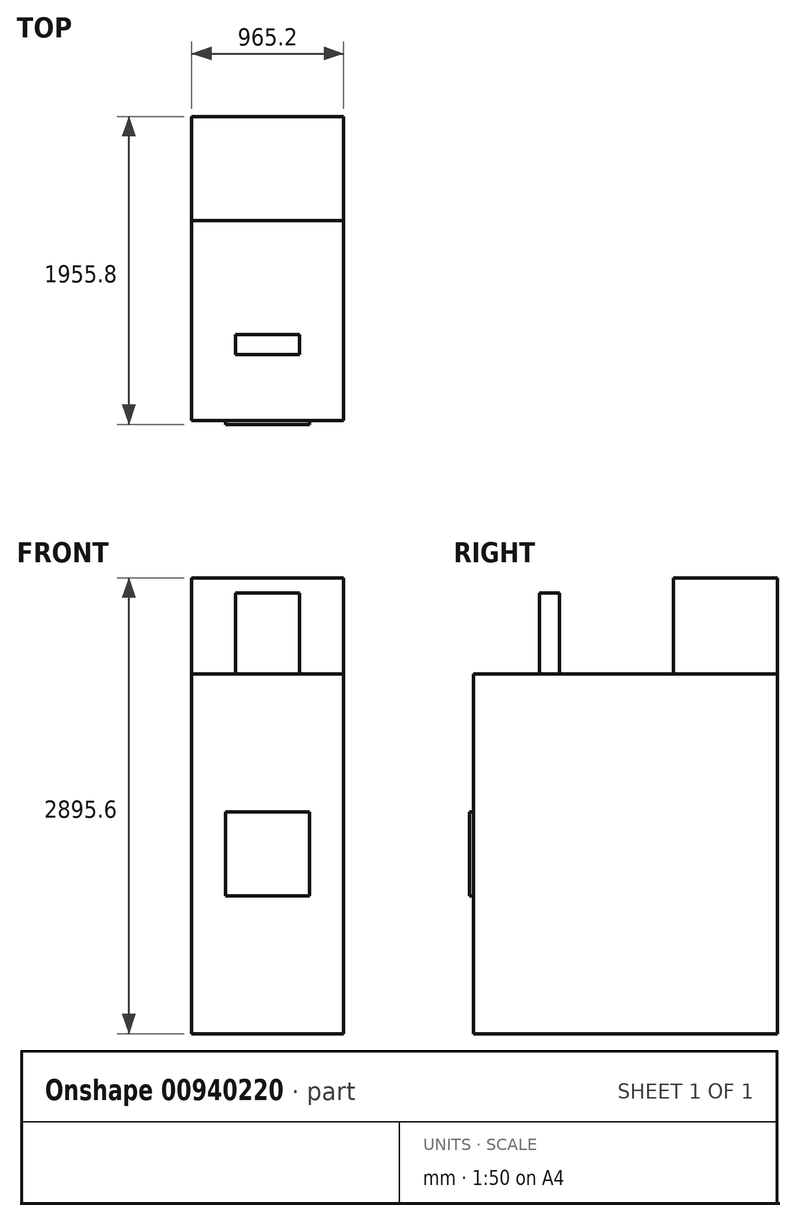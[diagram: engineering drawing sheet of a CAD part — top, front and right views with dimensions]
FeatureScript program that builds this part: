
annotation { "Feature Type Name" : "Feature", "Feature Type Description" : "" }
export const myFeature = defineFeature(function(context is Context, id is Id, definition is map)
    precondition{}
    {
        {
            var Q0;
            Q0=qCreatedBy(makeId("Front.planeOp"),FACE);
            var sketch = newSketch(context, id + "F0", { "sketchPlane" : qUnion([Q0])});
            skLineSegment(sketch, "E0.bottom", {"start": v(0, 0) * mm, "end": v(965.2, 0) * mm});
            skLineSegment(sketch, "E0.top", {"start": v(0, 2286) * mm, "end": v(965.2, 2286) * mm});
            skLineSegment(sketch, "E0.left", {"start": v(0, 0) * mm, "end": v(0, 2286) * mm});
            skLineSegment(sketch, "E0.right", {"start": v(965.2, 0) * mm, "end": v(965.2, 2286) * mm});
            skSolve(sketch);
        }
        {
            var Q0;
            Q0=makeQuery(id+"F0.imprint","IMPRINT",FACE,{"disambiguationData":[TD([[makeQuery(id+"F0.imprint","IMPRINT",EDGE,{"derivedFrom":sQuery(id+"F0.wireOp",EDGE,"E0.bottom")}),1.0]])]});
            extrude(context, id + "F1", {"entities" : qUnion([Q0]), "oppositeDirection" : true, "depth" : 965.2 * mm, "offsetDistance" : 25.4 * mm});
        }
        {
            var Q0;
            Q0=makeQuery(id+"F1.opExtrude","CAP_FACE",FACE,{"disambiguationData":[OSD([sQuery(id+"F0.wireOp",EDGE,"E0.bottom"),sQuery(id+"F0.wireOp",EDGE,"E0.top"),sQuery(id+"F0.wireOp",EDGE,"E0.left"),sQuery(id+"F0.wireOp",EDGE,"E0.right")])],"isStart":false});
            extrude(context, id + "F2", {"entities" : qUnion([Q0]), "depth" : 965.2 * mm, "offsetDistance" : 25.4 * mm});
        }
        {
            var Q0;
            Q0=makeQuery(id+"F1.opExtrude","SWEPT_FACE",FACE,{"disambiguationData":[OSD([sQuery(id+"F0.wireOp",EDGE,"E0.top")])]});
            var sketch = newSketch(context, id + "F3", { "sketchPlane" : qUnion([Q0])});
            skLineSegment(sketch, "E1.bottom", {"start": v(685.8, 419.1) * mm, "end": v(279.4, 419.1) * mm});
            skLineSegment(sketch, "E1.top", {"start": v(685.8, 546.1) * mm, "end": v(279.4, 546.1) * mm});
            skLineSegment(sketch, "E1.left", {"start": v(685.8, 419.1) * mm, "end": v(685.8, 546.1) * mm});
            skLineSegment(sketch, "E1.right", {"start": v(279.4, 419.1) * mm, "end": v(279.4, 546.1) * mm});
            skPoint(sketch, "E1.middle", {"position": v(482.6, 482.6) * mm});
            skPoint(sketch, "E1.middle.positionSnap0", {"position": v(965.2, 482.6) * mm});
            skPoint(sketch, "E1.middle.positionSnap1", {"position": v(482.6, 0) * mm});
            skPoint(sketch, "E1.centerSnap0", {"position": v(965.2, 482.6) * mm});
            skPoint(sketch, "E1.centerSnap1", {"position": v(482.6, 0) * mm});
            skSolve(sketch);
        }
        {
            var Q0;
            Q0=makeQuery(id+"F3.imprint","IMPRINT",FACE,{"disambiguationData":[TD([[makeQuery(id+"F3.imprint","IMPRINT",EDGE,{"derivedFrom":sQuery(id+"F3.wireOp",EDGE,"E1.bottom")}),-1.0]])]});
            extrude(context, id + "F4", {"entities" : qUnion([Q0]), "depth" : 513.08 * mm, "offsetDistance" : 25.4 * mm});
        }
        {
            var Q0;
            Q0=qCreatedBy(makeId("Front.planeOp"),FACE);
            var sketch = newSketch(context, id + "F5", { "sketchPlane" : qUnion([Q0])});
            skLineSegment(sketch, "E2", {"start": v(0, 0) * mm, "end": v(0, 1143) * mm, "construction": true});
            skLineSegment(sketch, "E3", {"start": v(0, 1143) * mm, "end": v(482.6, 1143) * mm, "construction": true});
            skLineSegment(sketch, "E4.bottom", {"start": v(749.3, 876.3) * mm, "end": v(215.9, 876.3) * mm});
            skLineSegment(sketch, "E4.top", {"start": v(749.3, 1409.7) * mm, "end": v(215.9, 1409.7) * mm});
            skLineSegment(sketch, "E4.left", {"start": v(749.3, 876.3) * mm, "end": v(749.3, 1409.7) * mm});
            skLineSegment(sketch, "E4.right", {"start": v(215.9, 876.3) * mm, "end": v(215.9, 1409.7) * mm});
            skPoint(sketch, "E4.middle", {"position": v(482.6, 1143) * mm});
            skSolve(sketch);
        }
        {
            var Q0;
            Q0=makeQuery(id+"F5.imprint","IMPRINT",FACE,{"disambiguationData":[TD([[makeQuery(id+"F5.imprint","IMPRINT",EDGE,{"derivedFrom":sQuery(id+"F5.wireOp",EDGE,"E4.bottom")}),-1.0]])]});
            extrude(context, id + "F6", {"entities" : qUnion([Q0]), "oppositeDirection" : true, "depth" : 482.6 * mm, "offsetDistance" : 25.4 * mm});
        }
        {
            var Q0;
            Q0=makeQuery(id+"F5.imprint","IMPRINT",FACE,{"disambiguationData":[TD([[makeQuery(id+"F5.imprint","IMPRINT",EDGE,{"derivedFrom":sQuery(id+"F5.wireOp",EDGE,"E4.bottom")}),-1.0]])]});
            extrude(context, id + "F7", {"entities" : qUnion([Q0]), "operationType" : NewBodyOperationType.ADD, "depth" : 25.4 * mm, "offsetDistance" : 25.4 * mm});
        }
        {
            var Q0;
            Q0=makeQuery(id+"F1.opExtrude","SWEPT_BODY",BODY,{"disambiguationData":[OSD([sQuery(id+"F0.wireOp",EDGE,"E0.bottom"),sQuery(id+"F0.wireOp",EDGE,"E0.top"),sQuery(id+"F0.wireOp",EDGE,"E0.left"),sQuery(id+"F0.wireOp",EDGE,"E0.right")])]});
            var Q1;
            Q1=makeQuery(id+"F2.opExtrude","SWEPT_BODY",BODY,{"disambiguationData":[OSD([sQuery(id+"F0.wireOp",EDGE,"E0.bottom"),sQuery(id+"F0.wireOp",EDGE,"E0.top"),sQuery(id+"F0.wireOp",EDGE,"E0.left"),sQuery(id+"F0.wireOp",EDGE,"E0.right")])]});
            booleanBodies(context, id + "F8", {"operationType" : BooleanOperationType.UNION, "tools" : qUnion([Q0, Q1])});
        }
        {
            var Q0;
            {var subQ0=sQuery(id+"F0.wireOp",EDGE,"E0.top");Q0=makeQuery(id+"F8.opBoolean","MERGE",FACE,{"derivedFrom":[makeQuery(id+"F1.opExtrude","SWEPT_FACE",FACE,{"disambiguationData":[OSD([subQ0])]}),makeQuery(id+"F2.opExtrude","SWEPT_FACE",FACE,{"disambiguationData":[OSD([subQ0])]})]});}
            var sketch = newSketch(context, id + "F9", { "sketchPlane" : qUnion([Q0])});
            skLineSegment(sketch, "E5.bottom", {"start": v(0, 1930.4) * mm, "end": v(965.2, 1930.4) * mm});
            skLineSegment(sketch, "E5.top", {"start": v(0, 1268.18) * mm, "end": v(965.2, 1268.18) * mm});
            skLineSegment(sketch, "E5.left", {"start": v(0, 1930.4) * mm, "end": v(0, 1268.18) * mm});
            skLineSegment(sketch, "E5.right", {"start": v(965.2, 1930.4) * mm, "end": v(965.2, 1268.18) * mm});
            skSolve(sketch);
        }
        {
            var Q0;
            Q0=makeQuery(id+"F9.imprint","IMPRINT",FACE,{"disambiguationData":[TD([[makeQuery(id+"F9.imprint","IMPRINT",EDGE,{"derivedFrom":sQuery(id+"F9.wireOp",EDGE,"E5.bottom")}),-1.0]])]});
            extrude(context, id + "F10", {"entities" : qUnion([Q0]), "depth" : 609.6 * mm, "offsetDistance" : 25.4 * mm});
        }
    });
